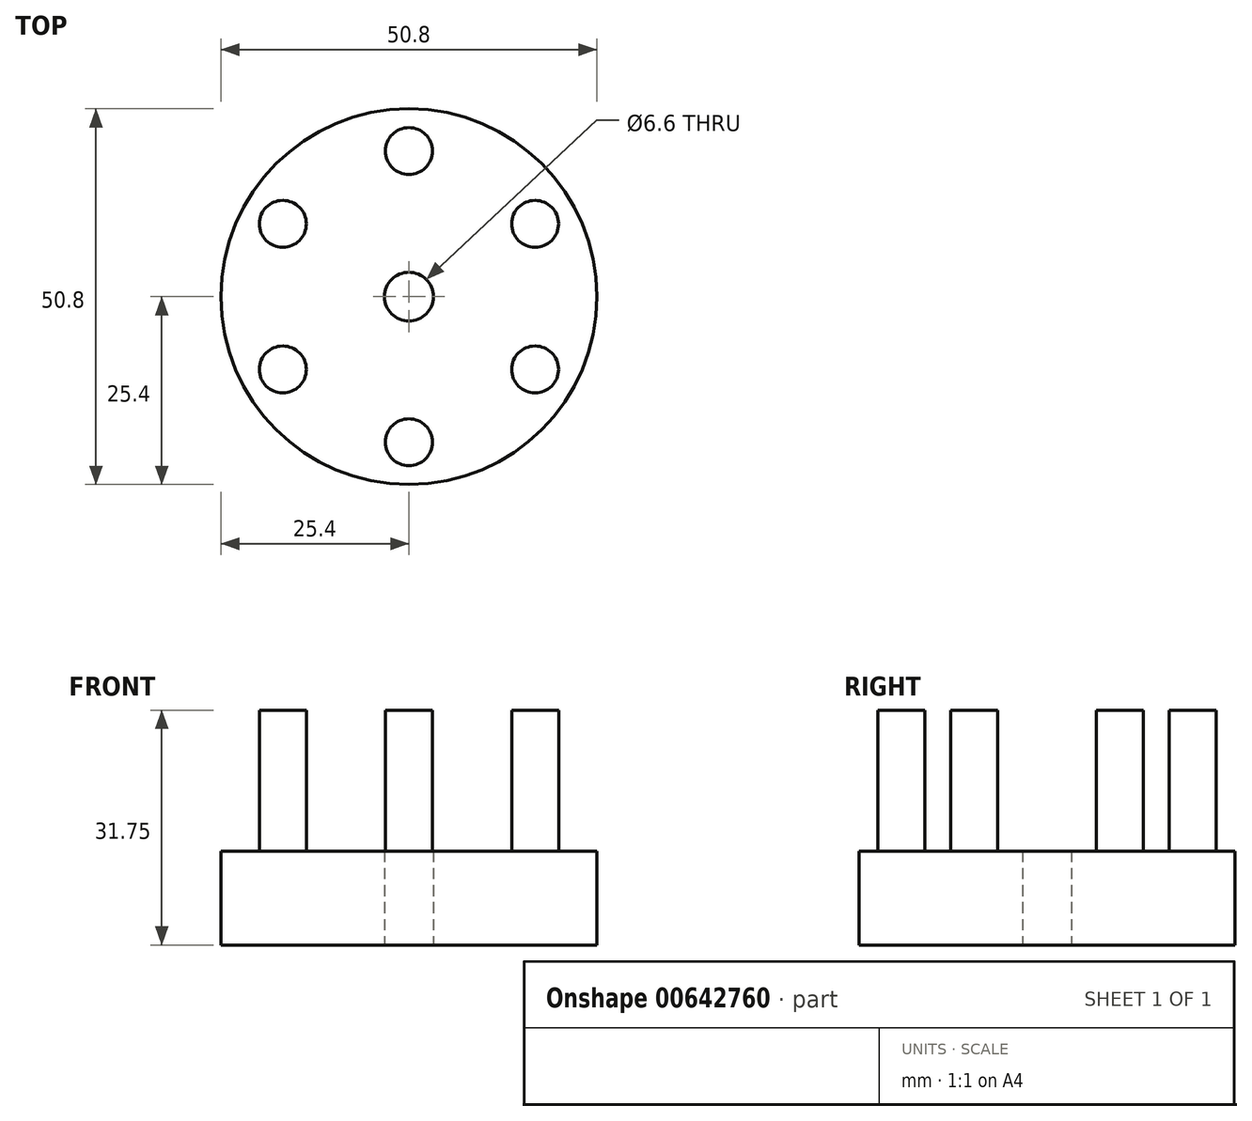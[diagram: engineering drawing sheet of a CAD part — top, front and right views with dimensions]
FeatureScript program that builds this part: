
annotation { "Feature Type Name" : "Feature", "Feature Type Description" : "" }
export const myFeature = defineFeature(function(context is Context, id is Id, definition is map)
    precondition{}
    {
        {
            var Q0;
            Q0=qCreatedBy(makeId("Top.planeOp"),FACE);
            var sketch = newSketch(context, id + "F0", { "sketchPlane" : qUnion([Q0])});
            skCircle(sketch, "E0", {"center": v(0, 0) * mm, "radius": 25.4 * mm});
            skSolve(sketch);
        }
        {
            var Q0;
            Q0 = qSketchRegion(id + "F0", true);
            extrude(context, id + "F1", {"entities" : qUnion([Q0]), "depth" : 12.7 * mm, "offsetDistance" : 25.4 * mm});
        }
        {
            var Q0;
            Q0=makeQuery(id+"F1.opExtrude","CAP_FACE",FACE,{"disambiguationData":[OSD([sQuery(id+"F0.wireOp",EDGE,"E0")])],"isStart":true});
            var sketch = newSketch(context, id + "F2", { "sketchPlane" : qUnion([Q0])});
            skCircle(sketch, "E1", {"center": v(0, 0) * mm, "radius": 3.3 * mm});
            skSolve(sketch);
        }
        {
            var Q0;
            Q0 = qSketchRegion(id + "F2", true);
            var Q1;
            Q1 = qSketchRegion(id + "FapnJaqTXfTuOeL_1", true);
            extrude(context, id + "F3", {"entities" : qUnion([Q0, Q1]), "operationType" : NewBodyOperationType.REMOVE, "oppositeDirection" : true, "depth" : 12.7 * mm, "offsetDistance" : 25.4 * mm});
        }
        {
            var Q0;
            Q0=makeQuery(id+"F1.opExtrude","CAP_FACE",FACE,{"disambiguationData":[OSD([sQuery(id+"F0.wireOp",EDGE,"E0")])],"isStart":false});
            var sketch = newSketch(context, id + "F4", { "sketchPlane" : qUnion([Q0])});
            skCircle(sketch, "E2", {"center": v(0, 19.69) * mm, "radius": 3.17 * mm});
            skCircle(sketch, "E3.1.0", {"center": v(-17.05, 9.84) * mm, "radius": 3.17 * mm});
            skCircle(sketch, "E3.2.0", {"center": v(-17.05, -9.84) * mm, "radius": 3.17 * mm});
            skCircle(sketch, "E3.3.0", {"center": v(0, -19.69) * mm, "radius": 3.17 * mm});
            skCircle(sketch, "E3.4.0", {"center": v(17.05, -9.84) * mm, "radius": 3.17 * mm});
            skCircle(sketch, "E3.5.0", {"center": v(17.05, 9.84) * mm, "radius": 3.17 * mm});
            skPoint(sketch, "E3.center", {"position": v(0, 0) * mm});
            skSolve(sketch);
        }
        {
            var Q0;
            Q0 = qSketchRegion(id + "F4", true);
            extrude(context, id + "F5", {"entities" : qUnion([Q0]), "operationType" : NewBodyOperationType.ADD, "depth" : 19.05 * mm, "offsetDistance" : 25.4 * mm});
        }
    });
